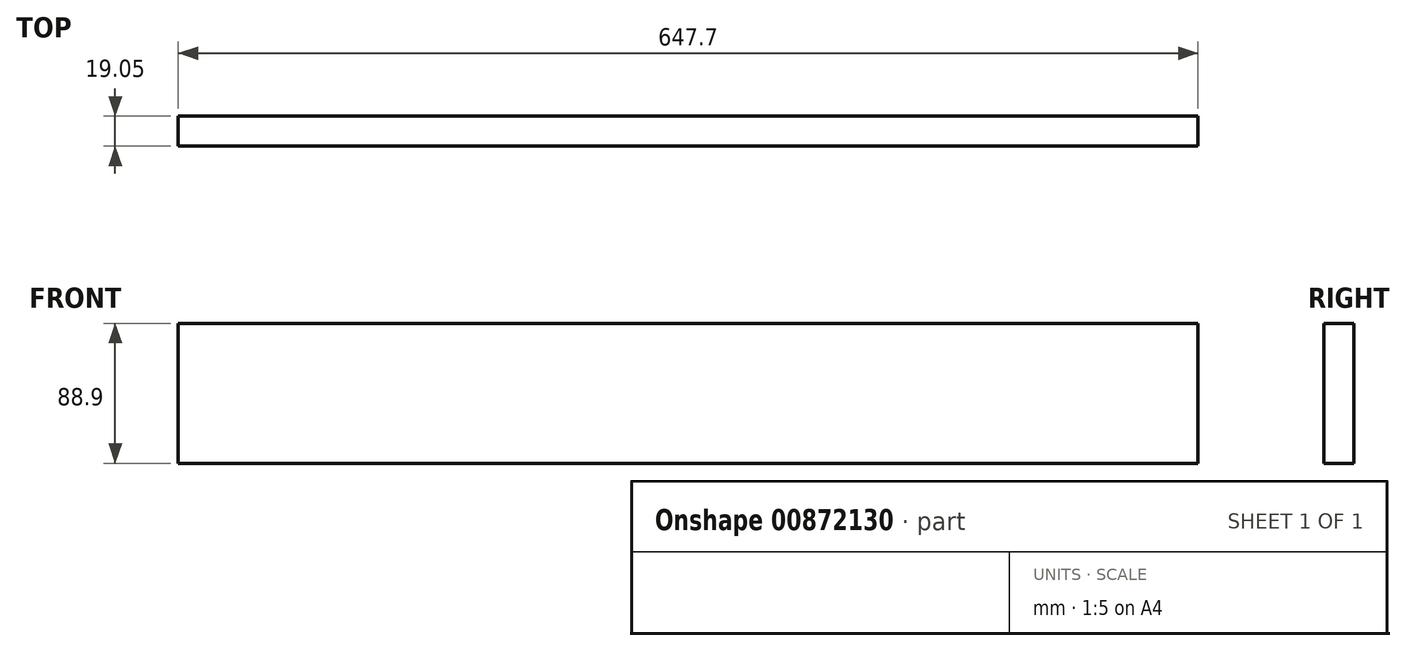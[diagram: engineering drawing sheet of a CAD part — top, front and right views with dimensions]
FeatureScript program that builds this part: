
annotation { "Feature Type Name" : "Feature", "Feature Type Description" : "" }
export const myFeature = defineFeature(function(context is Context, id is Id, definition is map)
    precondition{}
    {
        {
            var Q0;
            Q0=qCreatedBy(makeId("Front.planeOp"),FACE);
            var sketch = newSketch(context, id + "F0", { "sketchPlane" : qUnion([Q0])});
            skLineSegment(sketch, "E0.bottom", {"start": v(0, 0) * mm, "end": v(-647.7, 0) * mm});
            skLineSegment(sketch, "E0.top", {"start": v(0, 88.9) * mm, "end": v(-647.7, 88.9) * mm});
            skLineSegment(sketch, "E0.left", {"start": v(0, 0) * mm, "end": v(0, 88.9) * mm});
            skLineSegment(sketch, "E0.right", {"start": v(-647.7, 0) * mm, "end": v(-647.7, 88.9) * mm});
            skSolve(sketch);
        }
        {
            var Q0;
            Q0=makeQuery(id+"F0.imprint","IMPRINT",FACE,{"disambiguationData":[TD([[makeQuery(id+"F0.imprint","IMPRINT",EDGE,{"derivedFrom":sQuery(id+"F0.wireOp",EDGE,"E0.bottom")}),-1.0]])]});
            extrude(context, id + "F1", {"entities" : qUnion([Q0]), "depth" : 19.05 * mm, "offsetDistance" : 25.4 * mm});
        }
    });
